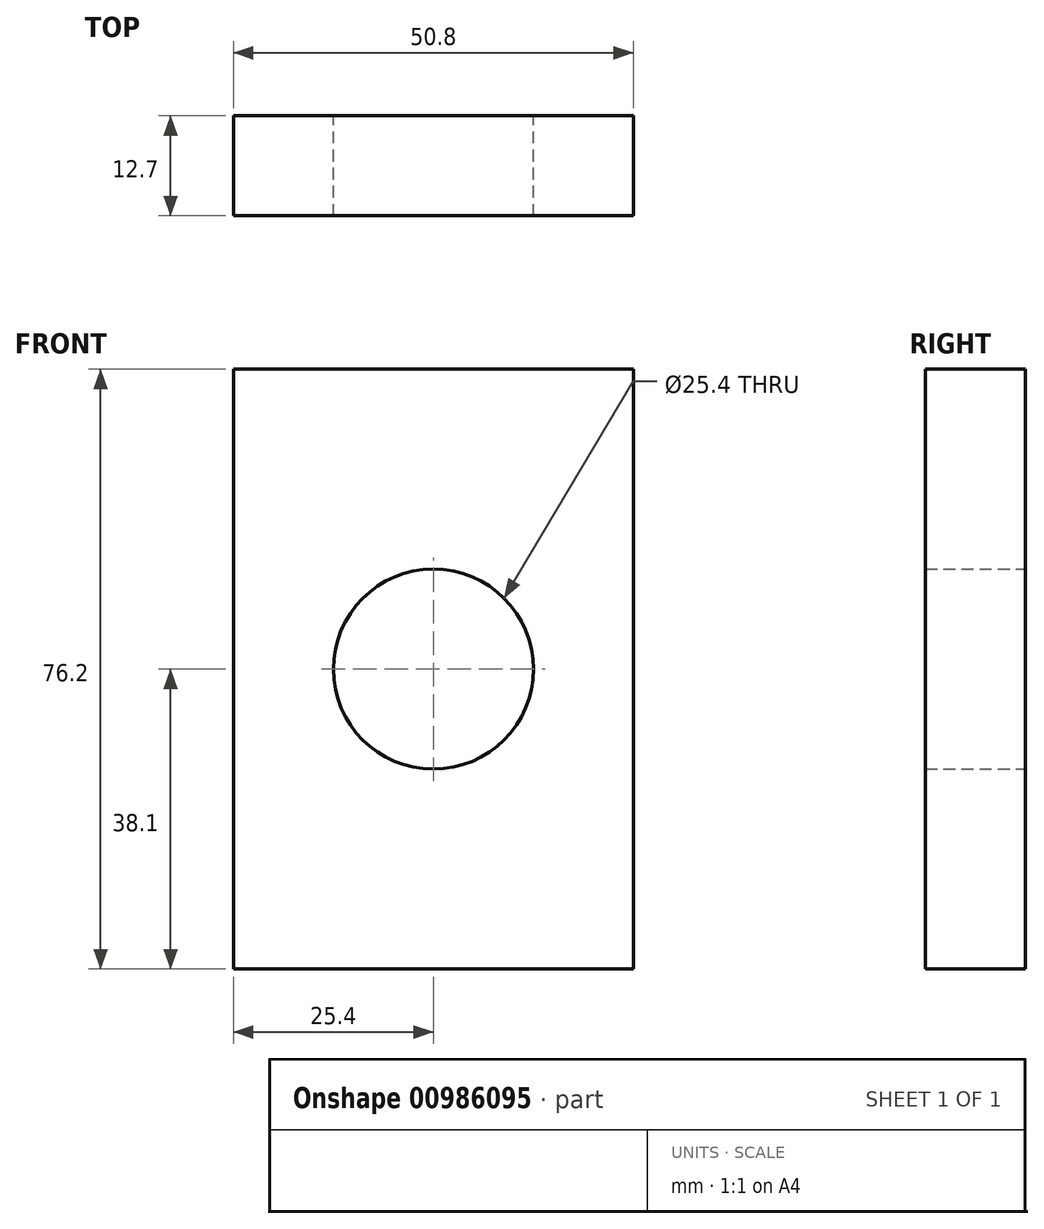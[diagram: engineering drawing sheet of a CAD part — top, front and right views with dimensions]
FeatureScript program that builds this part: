
annotation { "Feature Type Name" : "Feature", "Feature Type Description" : "" }
export const myFeature = defineFeature(function(context is Context, id is Id, definition is map)
    precondition{}
    {
        {
            var Q0;
            Q0=qCreatedBy(makeId("Front.planeOp"),FACE);
            var sketch = newSketch(context, id + "F0", { "sketchPlane" : qUnion([Q0])});
            skLineSegment(sketch, "E0.bottom", {"start": v(25.4, -38.1) * mm, "end": v(-25.4, -38.1) * mm});
            skLineSegment(sketch, "E0.top", {"start": v(25.4, 38.1) * mm, "end": v(-25.4, 38.1) * mm});
            skLineSegment(sketch, "E0.left", {"start": v(25.4, -38.1) * mm, "end": v(25.4, 38.1) * mm});
            skLineSegment(sketch, "E0.right", {"start": v(-25.4, -38.1) * mm, "end": v(-25.4, 38.1) * mm});
            skPoint(sketch, "E0.middle", {"position": v(0, 0) * mm});
            skCircle(sketch, "E1", {"center": v(0, 0) * mm, "radius": 12.7 * mm});
            skSolve(sketch);
        }
        {
            var Q0;
            Q0 = qSketchRegion(id + "F0", true);
            extrude(context, id + "F1", {"entities" : qUnion([Q0]), "depth" : 12.7 * mm, "offsetDistance" : 25.4 * mm});
        }
    });
